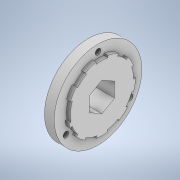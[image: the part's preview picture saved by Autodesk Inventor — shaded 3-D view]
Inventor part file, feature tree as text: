
AUTODESK INVENTOR PART (.ipt)
format: ipt  version: 2021 (Build 250183000, 183)  size: 287,232 bytes
history: native  units: mm
features: sketch x6, extrude x5, plane x1, projected_geometry x1
ambient origin geometry x8: Origin, YZ Plane, XZ Plane, XY Plane, X Axis, Y Axis, Z Axis, Center Point
bodies: Solid1 (feature_tree)
feature tree (13):
  extrude  "Extrusion1"  Depth=7.5mm
  extrude  "Extrusion2"  Depth=10.25mm
  extrude  "Extrusion3"  Depth=5.0mm TaperAngle=360.0deg
  sketch  "Sketch4"  dims[d13=5.0mm d14=0.0mm d15=35.0mm]
  plane  "Work Plane1"
  sketch  "Sketch5"  dims[d16=33.0mm d42=2.0mm d43=0.0mm]
  extrude  "Extrusion6"  Depth=5.0mm
  extrude  "Extrusion7"  Depth=2.0mm TaperAngle=0.0deg
  sketch  "Sketch1"  dims[d0=7.5mm d1=30.0mm]
  sketch  "Sketch2"  dims[d2=10.25mm d3=0.0mm d4=45.0mm]
  sketch  "Sketch3"  dims[d5=5.0mm d6=0.0mm d9=30.0mm d11=360.0deg]
  sketch  "Sketch6"  dims[d44=34.5mm d45=32.5mm d46=1.9mm d47=0.0mm]
  projected_geometry  "Projected Loop1"
